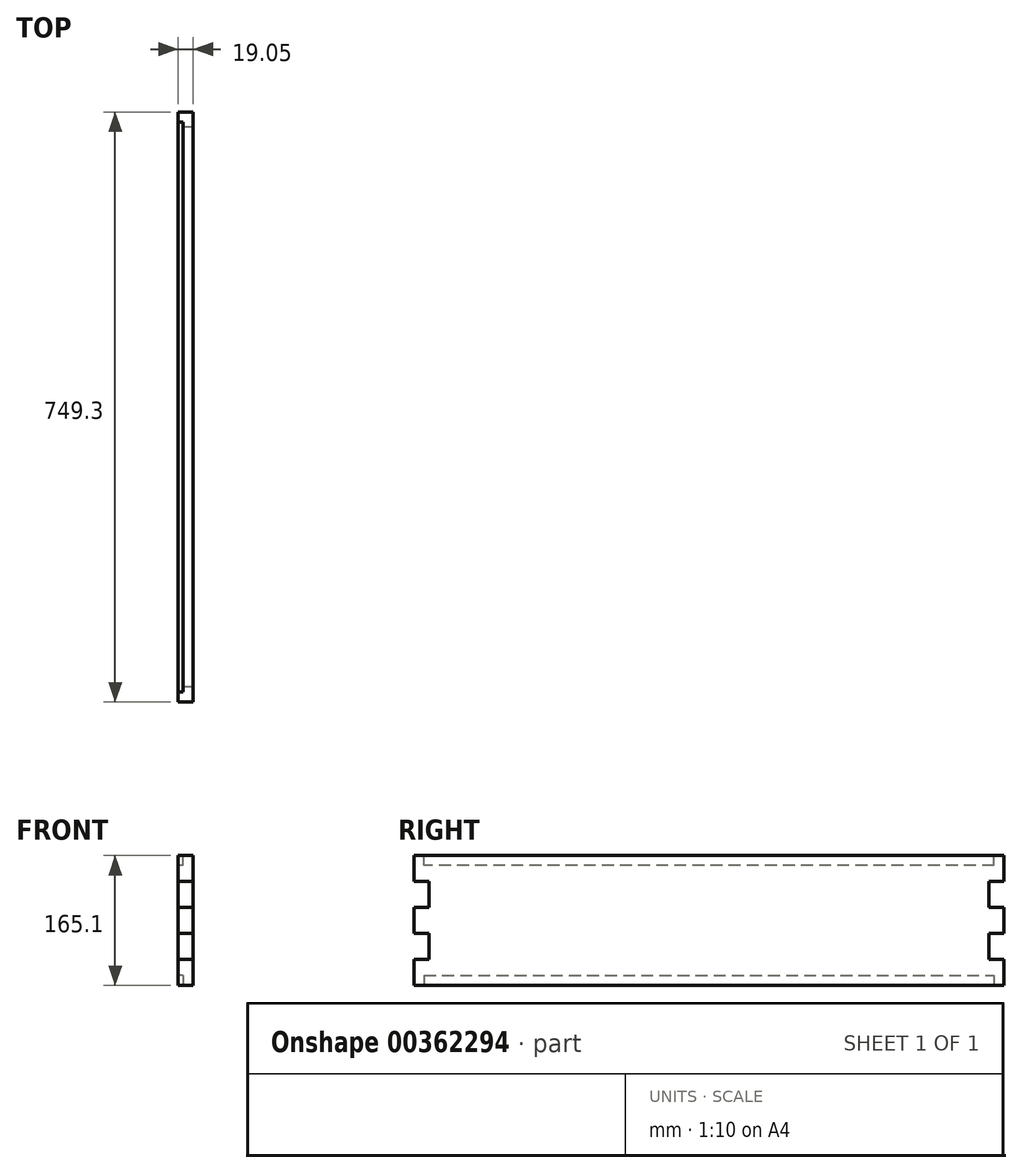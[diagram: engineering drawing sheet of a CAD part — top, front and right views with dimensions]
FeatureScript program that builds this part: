
annotation { "Feature Type Name" : "Feature", "Feature Type Description" : "" }
export const myFeature = defineFeature(function(context is Context, id is Id, definition is map)
    precondition{}
    {
        {
            var Q0;
            Q0=qCreatedBy(makeId("Right.planeOp"),FACE);
            var sketch = newSketch(context, id + "F0", { "sketchPlane" : qUnion([Q0])});
            skLineSegment(sketch, "E0.bottom", {"start": v(-583.25, 72.29) * mm, "end": v(-564.2, 72.29) * mm});
            skLineSegment(sketch, "E0.top", {"start": v(-583.25, -92.81) * mm, "end": v(-564.2, -92.81) * mm});
            skLineSegment(sketch, "E0.left", {"start": v(-583.25, 72.29) * mm, "end": v(-583.25, 39.27) * mm});
            skLineSegment(sketch, "E0.right", {"start": v(166.05, 72.29) * mm, "end": v(166.05, 39.27) * mm});
            skLineSegment(sketch, "E1", {"start": v(-564.2, 72.29) * mm, "end": v(147, 72.29) * mm});
            skLineSegment(sketch, "E2", {"start": v(-564.2, -92.81) * mm, "end": v(147, -92.81) * mm});
            skLineSegment(sketch, "E3", {"start": v(-583.25, -59.8) * mm, "end": v(-564.2, -59.8) * mm});
            skLineSegment(sketch, "E4", {"start": v(-583.25, -26.77) * mm, "end": v(-564.2, -26.77) * mm});
            skLineSegment(sketch, "E5", {"start": v(-583.25, 6.25) * mm, "end": v(-564.2, 6.25) * mm});
            skLineSegment(sketch, "E6", {"start": v(-583.25, 39.27) * mm, "end": v(-564.2, 39.27) * mm});
            skLineSegment(sketch, "E7", {"start": v(-564.2, 39.27) * mm, "end": v(-564.2, 6.25) * mm});
            skLineSegment(sketch, "E8", {"start": v(-583.25, 6.25) * mm, "end": v(-583.25, -26.77) * mm});
            skLineSegment(sketch, "E9", {"start": v(-564.2, 6.25) * mm, "end": v(-564.2, 6.25) * mm});
            skLineSegment(sketch, "E10", {"start": v(-564.2, -26.77) * mm, "end": v(-564.2, -59.8) * mm});
            skLineSegment(sketch, "E11", {"start": v(-583.25, -59.8) * mm, "end": v(-583.25, -92.81) * mm});
            skLineSegment(sketch, "E12", {"start": v(147, 72.29) * mm, "end": v(147, 72.29) * mm});
            skLineSegment(sketch, "E13", {"start": v(147, 72.29) * mm, "end": v(166.05, 72.29) * mm});
            skLineSegment(sketch, "E14", {"start": v(166.05, -59.8) * mm, "end": v(166.05, -92.81) * mm});
            skLineSegment(sketch, "E15", {"start": v(-564.2, 6.25) * mm, "end": v(-564.2, -26.77) * mm});
            skLineSegment(sketch, "E16", {"start": v(147, -92.81) * mm, "end": v(166.05, -92.81) * mm});
            skLineSegment(sketch, "E17", {"start": v(166.05, 39.27) * mm, "end": v(147, 39.27) * mm});
            skLineSegment(sketch, "E18", {"start": v(166.05, -59.8) * mm, "end": v(147, -59.8) * mm});
            skLineSegment(sketch, "E19", {"start": v(-564.2, 59.59) * mm, "end": v(147, 59.59) * mm});
            skLineSegment(sketch, "E20", {"start": v(-564.2, -80.11) * mm, "end": v(147, -80.11) * mm});
            skLineSegment(sketch, "E21", {"start": v(147, 59.59) * mm, "end": v(153.35, 59.59) * mm});
            skLineSegment(sketch, "E22", {"start": v(153.35, 59.59) * mm, "end": v(153.35, 72.29) * mm});
            skLineSegment(sketch, "E23", {"start": v(153.35, 72.29) * mm, "end": v(147, 72.29) * mm});
            skLineSegment(sketch, "E24", {"start": v(147, 59.59) * mm, "end": v(147, -10.26) * mm});
            skLineSegment(sketch, "E25", {"start": v(153.35, -80.11) * mm, "end": v(153.35, -92.81) * mm});
            skLineSegment(sketch, "E26", {"start": v(153.35, -92.81) * mm, "end": v(147, -92.81) * mm});
            skLineSegment(sketch, "E27", {"start": v(153.35, -80.11) * mm, "end": v(147, -80.11) * mm});
            skLineSegment(sketch, "E28", {"start": v(-564.2, 59.59) * mm, "end": v(-570.55, 59.59) * mm});
            skLineSegment(sketch, "E29", {"start": v(-570.55, 59.59) * mm, "end": v(-570.55, 72.29) * mm});
            skLineSegment(sketch, "E30", {"start": v(-570.55, 72.29) * mm, "end": v(-564.2, 72.29) * mm});
            skLineSegment(sketch, "E31", {"start": v(-570.55, -80.11) * mm, "end": v(-570.55, -92.81) * mm});
            skLineSegment(sketch, "E32", {"start": v(-570.55, -92.81) * mm, "end": v(-564.2, -92.81) * mm});
            skLineSegment(sketch, "E33", {"start": v(-564.2, -80.11) * mm, "end": v(-570.55, -80.11) * mm});
            skLineSegment(sketch, "E34", {"start": v(-564.2, -59.8) * mm, "end": v(-564.2, -80.11) * mm});
            skLineSegment(sketch, "E35", {"start": v(147, -10.26) * mm, "end": v(147, -80.11) * mm});
            skLineSegment(sketch, "E36", {"start": v(147, -10.26) * mm, "end": v(147, 6.25) * mm});
            skLineSegment(sketch, "E37", {"start": v(147, 6.25) * mm, "end": v(166.05, 6.25) * mm});
            skLineSegment(sketch, "E38", {"start": v(166.05, 6.25) * mm, "end": v(166.05, -26.77) * mm});
            skLineSegment(sketch, "E39", {"start": v(166.05, -26.77) * mm, "end": v(147, -26.77) * mm});
            skSolve(sketch);
        }
        {
            var Q0;
            Q0 = qSketchRegion(id + "F0", true);
            extrude(context, id + "F1", {"entities" : qUnion([Q0]), "depth" : 19.05 * mm});
        }
        {
            var Q0;
            {var subQ0=sQuery(id+"F0.wireOp",EDGE,"E1");Q0=makeQuery(id+"F0.imprint","IMPRINT",FACE,{"disambiguationData":[TD([[makeQuery(id+"F0.imprint","IMPRINT",EDGE,{"derivedFrom":subQ0}),-1.0]])]});}
            extrude(context, id + "F2", {"entities" : qUnion([Q0]), "operationType" : NewBodyOperationType.REMOVE, "depth" : 6.35 * mm});
        }
        {
            var Q0;
            {var subQ0=sQuery(id+"F0.wireOp",EDGE,"E2");Q0=makeQuery(id+"F0.imprint","IMPRINT",FACE,{"disambiguationData":[TD([[makeQuery(id+"F0.imprint","IMPRINT",EDGE,{"derivedFrom":subQ0}),1.0]])]});}
            extrude(context, id + "F3", {"entities" : qUnion([Q0]), "operationType" : NewBodyOperationType.REMOVE, "depth" : 6.35 * mm});
        }
    });
